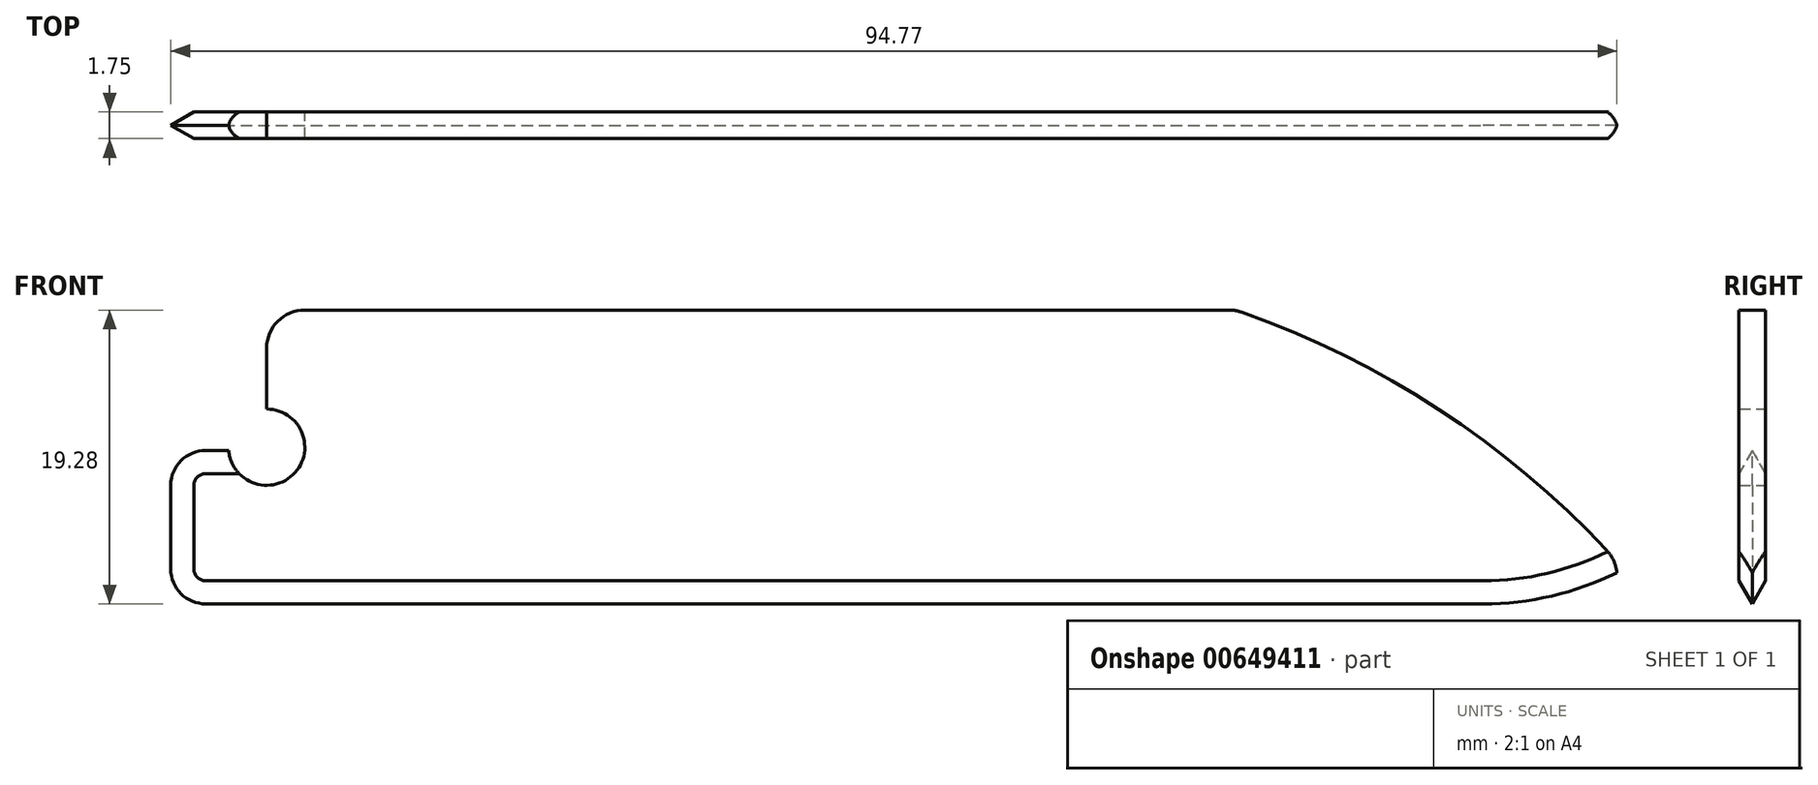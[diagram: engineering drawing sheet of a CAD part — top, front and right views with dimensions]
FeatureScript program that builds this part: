
annotation { "Feature Type Name" : "Feature", "Feature Type Description" : "" }
export const myFeature = defineFeature(function(context is Context, id is Id, definition is map)
    precondition{}
    {
        {
            var Q0;
            Q0=qCreatedBy(makeId("Front.planeOp"),FACE);
            var sketch = newSketch(context, id + "F0", { "sketchPlane" : qUnion([Q0])});
            skLineSegment(sketch, "E0.bottom", {"start": v(47.5, -9.75) * mm, "end": v(-47.5, -9.75) * mm});
            skLineSegment(sketch, "E0.top", {"start": v(47.5, 9.75) * mm, "end": v(-47.5, 9.75) * mm});
            skLineSegment(sketch, "E0.left", {"start": v(47.5, -9.75) * mm, "end": v(47.5, 9.75) * mm});
            skLineSegment(sketch, "E0.right", {"start": v(-47.5, -9.75) * mm, "end": v(-47.5, 9.75) * mm});
            skPoint(sketch, "E0.middle", {"position": v(0, 0) * mm});
            skLineSegment(sketch, "E1", {"start": v(-41, 9.75) * mm, "end": v(-41, 0.75) * mm});
            skLineSegment(sketch, "E2", {"start": v(-41, 0.75) * mm, "end": v(-47.5, 0.75) * mm});
            skCircle(sketch, "E3", {"center": v(-41, 0.75) * mm, "radius": 2.5 * mm});
            skLineSegment(sketch, "E4", {"start": v(-36, 9.75) * mm, "end": v(-36, -6.25) * mm});
            skLineSegment(sketch, "E5", {"start": v(-36, -6.25) * mm, "end": v(-47.5, -6.25) * mm});
            skLineSegment(sketch, "E6", {"start": v(-36, -6.25) * mm, "end": v(-36, -9.75) * mm});
            skArc(sketch, "E7", {"start": v(47.5, -6.75) * mm, "mid": v(36.05, 3.09) * mm, "end": v(22.5, 9.75) * mm});
            skLineSegment(sketch, "E8", {"start": v(-47.5, 9.75) * mm, "end": v(22.5, 9.75) * mm});
            skLineSegment(sketch, "E9", {"start": v(47.5, -6.75) * mm, "end": v(47.5, -9.75) * mm});
            skSolve(sketch);
        }
        {
            var Q0;
            {var subQ10=sQuery(id+"F0.wireOp",EDGE,"E4");Q0=makeQuery(id+"F0.imprint","IMPRINT",FACE,{"disambiguationData":[TD([[makeQuery(id+"F0.imprint","IMPRINT",EDGE,{"derivedFrom":subQ10}),-1.0]])]});}
            var Q1;
            {var subQ1=sQuery(id+"F0.wireOp",EDGE,"E4");Q1=makeQuery(id+"F0.imprint","IMPRINT",FACE,{"disambiguationData":[TD([[makeQuery(id+"F0.imprint","IMPRINT",EDGE,{"derivedFrom":subQ1}),1.0]])]});}
            var Q2;
            {var subQ1=sQuery(id+"F0.wireOp",EDGE,"E0.right");var subQ5=sQuery(id+"F0.wireOp",EDGE,"E8");var subQ9=makeQuery(id+"F0.imprint","INTERSECT",VERTEX,{"derivedFrom":[subQ1,subQ5]});Q2=makeQuery(id+"F0.imprint","IMPRINT",FACE,{"disambiguationData":[TD([[makeQuery(id+"F0.imprint","IMPRINT",EDGE,{"disambiguationData":[TD([[subQ9,1.0]])],"derivedFrom":subQ1}),-1.0]])]});}
            extrude(context, id + "F1", {"entities" : qUnion([Q0, Q1, Q2]), "depth" : 1.75 * mm, "offsetDistance" : 25 * mm});
        }
        {
            var Q0;
            Q0=makeQuery(id+"F1.opExtrude","SWEPT_EDGE",EDGE,{"disambiguationData":[OSD([sQuery(id+"F0.wireOp",EDGE,"E4"),sQuery(id+"F0.wireOp",EDGE,"E5"),sQuery(id+"F0.wireOp",EDGE,"E6")])]});
            var Q1;
            Q1=makeQuery(id+"F1.opExtrude","SWEPT_EDGE",EDGE,{"disambiguationData":[OSD([sQuery(id+"F0.wireOp",EDGE,"E0.right"),sQuery(id+"F0.wireOp",EDGE,"E5")])]});
            var Q2;
            Q2=makeQuery(id+"F1.opExtrude","SWEPT_EDGE",EDGE,{"disambiguationData":[OSD([sQuery(id+"F0.wireOp",EDGE,"E0.top"),sQuery(id+"F0.wireOp",EDGE,"E0.right")])]});
            var Q3;
            Q3=makeQuery(id+"F1.opExtrude","SWEPT_EDGE",EDGE,{"disambiguationData":[OSD([sQuery(id+"F0.wireOp",EDGE,"E0.top"),sQuery(id+"F0.wireOp",EDGE,"E7"),sQuery(id+"F0.wireOp",EDGE,"E8")])]});
            var Q4;
            Q4=makeQuery(id+"F1.opExtrude","SWEPT_EDGE",EDGE,{"disambiguationData":[OSD([sQuery(id+"F0.wireOp",EDGE,"E0.left"),sQuery(id+"F0.wireOp",EDGE,"E7"),sQuery(id+"F0.wireOp",EDGE,"E9")])]});
            fillet(context, id + "F2", {"entities" : qUnion([Q0, Q1, Q2, Q3, Q4]), "radius" : 2.5 * mm, "tangentPropagation" : true, "allowEdgeOverflow" : false});
        }
        {
            var Q0;
            Q0=makeQuery(id+"F1.opExtrude","SWEPT_EDGE",EDGE,{"disambiguationData":[OSD([sQuery(id+"F0.wireOp",EDGE,"E0.bottom"),sQuery(id+"F0.wireOp",EDGE,"E9")])]});
            fillet(context, id + "F3", {"entities" : qUnion([Q0]), "radius" : 20 * mm, "tangentPropagation" : true, "allowEdgeOverflow" : false});
        }
        {
            var Q0;
            Q0=makeQuery(id+"F1.opExtrude","CAP_EDGE",EDGE,{"disambiguationData":[OSD([sQuery(id+"F0.wireOp",EDGE,"E0.bottom")])],"isStart":false});
            var Q1;
            Q1=makeQuery(id+"F1.opExtrude","CAP_EDGE",EDGE,{"disambiguationData":[OSD([sQuery(id+"F0.wireOp",EDGE,"E0.bottom")])],"isStart":true});
            chamfer(context, id + "F4", {"entities" : qUnion([Q0, Q1]), "chamferType" : ChamferType.OFFSET_ANGLE, "width" : 1 * mm, "oppositeDirection" : false, "angle" : 60 * degree, "tangentPropagation" : true});
        }
    });
